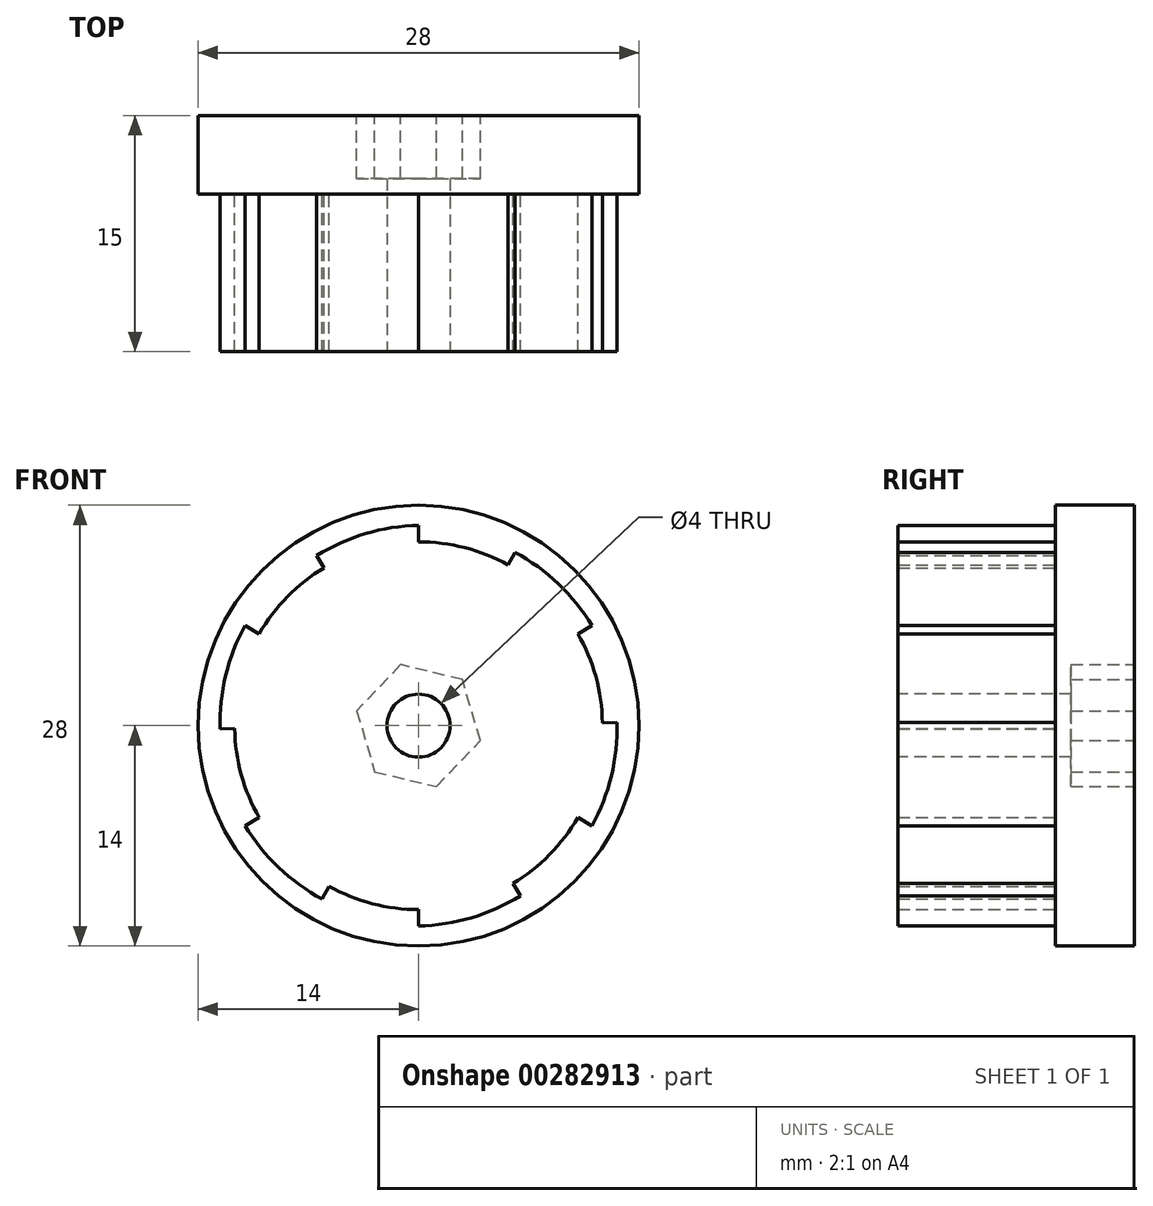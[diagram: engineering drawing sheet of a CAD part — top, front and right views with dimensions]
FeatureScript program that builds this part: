
annotation { "Feature Type Name" : "Feature", "Feature Type Description" : "" }
export const myFeature = defineFeature(function(context is Context, id is Id, definition is map)
    precondition{}
    {
        {
            var Q0;
            Q0=qCreatedBy(makeId("Front.planeOp"),FACE);
            var sketch = newSketch(context, id + "F0", { "sketchPlane" : qUnion([Q0])});
            skCircle(sketch, "E0", {"center": v(0, 0) * mm, "radius": 12.9 * mm, "construction": true});
            skCircle(sketch, "E1", {"center": v(0, 0) * mm, "radius": 14 * mm, "construction": true});
            skCircle(sketch, "E2", {"center": v(0, 0) * mm, "radius": 11.9 * mm, "construction": true});
            skCircle(sketch, "E3", {"center": v(0, 0) * mm, "radius": 11.68 * mm});
            skLineSegment(sketch, "E4", {"start": v(0, 0) * mm, "end": v(0, 14) * mm, "construction": true});
            skLineSegment(sketch, "E5", {"start": v(0, 0) * mm, "end": v(-7.2, 12.01) * mm, "construction": true});
            skLineSegment(sketch, "E6", {"start": v(-6, 10.02) * mm, "end": v(-6.47, 10.8) * mm});
            skLineSegment(sketch, "E7", {"start": v(0, 11.68) * mm, "end": v(0, 12.72) * mm});
            skArc(sketch, "E8", {"start": v(0, 12.72) * mm, "mid": v(-3.36, 12.2) * mm, "end": v(-6.47, 10.8) * mm});
            skLineSegment(sketch, "E9.1.0", {"start": v(-11.68, -0.19) * mm, "end": v(-12.6, -0.2) * mm});
            skArc(sketch, "E9.1.1", {"start": v(-11.02, 6.36) * mm, "mid": v(-12.24, 3.19) * mm, "end": v(-12.6, -0.2) * mm});
            skLineSegment(sketch, "E9.1.2", {"start": v(-10.12, 5.84) * mm, "end": v(-11.02, 6.36) * mm});
            skLineSegment(sketch, "E9.2.0", {"start": v(-5.68, -10.2) * mm, "end": v(-6.12, -11) * mm});
            skArc(sketch, "E9.2.1", {"start": v(-11.02, -6.36) * mm, "mid": v(-8.88, -9.01) * mm, "end": v(-6.12, -11) * mm});
            skLineSegment(sketch, "E9.2.2", {"start": v(-10.12, -5.84) * mm, "end": v(-11.02, -6.36) * mm});
            skLineSegment(sketch, "E9.3.0", {"start": v(6, -10.02) * mm, "end": v(6.47, -10.8) * mm});
            skArc(sketch, "E9.3.1", {"start": v(0, -12.72) * mm, "mid": v(3.36, -12.2) * mm, "end": v(6.47, -10.8) * mm});
            skLineSegment(sketch, "E9.3.2", {"start": v(0, -11.68) * mm, "end": v(0, -12.72) * mm});
            skLineSegment(sketch, "E9.4.0", {"start": v(11.68, 0.19) * mm, "end": v(12.6, 0.2) * mm});
            skArc(sketch, "E9.4.1", {"start": v(11.02, -6.36) * mm, "mid": v(12.24, -3.19) * mm, "end": v(12.6, 0.2) * mm});
            skLineSegment(sketch, "E9.4.2", {"start": v(10.12, -5.84) * mm, "end": v(11.02, -6.36) * mm});
            skLineSegment(sketch, "E9.5.0", {"start": v(5.68, 10.2) * mm, "end": v(6.12, 11) * mm});
            skArc(sketch, "E9.5.1", {"start": v(11.02, 6.36) * mm, "mid": v(8.88, 9.01) * mm, "end": v(6.12, 11) * mm});
            skLineSegment(sketch, "E9.5.2", {"start": v(10.12, 5.84) * mm, "end": v(11.02, 6.36) * mm});
            skSolve(sketch);
        }
        {
            var Q0;
            Q0 = qSketchRegion(id + "F0", true);
            extrude(context, id + "F1", {"entities" : qUnion([Q0]), "depth" : 10 * mm});
        }
        {
            var Q0;
            Q0=makeQuery(id+"F1.opExtrude","CAP_FACE",FACE,{"disambiguationData":[OSD([sQuery(id+"F0.wireOp",EDGE,"E3"),sQuery(id+"F0.wireOp",EDGE,"E6"),sQuery(id+"F0.wireOp",EDGE,"E7"),sQuery(id+"F0.wireOp",EDGE,"E8"),sQuery(id+"F0.wireOp",EDGE,"E9.1.0"),sQuery(id+"F0.wireOp",EDGE,"E9.1.1"),sQuery(id+"F0.wireOp",EDGE,"E9.1.2"),sQuery(id+"F0.wireOp",EDGE,"E9.2.0"),sQuery(id+"F0.wireOp",EDGE,"E9.2.1"),sQuery(id+"F0.wireOp",EDGE,"E9.2.2"),sQuery(id+"F0.wireOp",EDGE,"E9.3.0"),sQuery(id+"F0.wireOp",EDGE,"E9.3.1"),sQuery(id+"F0.wireOp",EDGE,"E9.3.2"),sQuery(id+"F0.wireOp",EDGE,"E9.4.0"),sQuery(id+"F0.wireOp",EDGE,"E9.4.1"),sQuery(id+"F0.wireOp",EDGE,"E9.4.2"),sQuery(id+"F0.wireOp",EDGE,"E9.5.0"),sQuery(id+"F0.wireOp",EDGE,"E9.5.1"),sQuery(id+"F0.wireOp",EDGE,"E9.5.2")])],"isStart":false});
            var sketch = newSketch(context, id + "F2", { "sketchPlane" : qUnion([Q0])});
            skCircle(sketch, "E10", {"center": v(0, 0) * mm, "radius": 2 * mm});
            skSolve(sketch);
        }
        {
            var Q0;
            Q0=makeQuery(id+"F1.opExtrude","CAP_FACE",FACE,{"disambiguationData":[OSD([sQuery(id+"F0.wireOp",EDGE,"E3"),sQuery(id+"F0.wireOp",EDGE,"E6"),sQuery(id+"F0.wireOp",EDGE,"E7"),sQuery(id+"F0.wireOp",EDGE,"E8"),sQuery(id+"F0.wireOp",EDGE,"E9.1.0"),sQuery(id+"F0.wireOp",EDGE,"E9.1.1"),sQuery(id+"F0.wireOp",EDGE,"E9.1.2"),sQuery(id+"F0.wireOp",EDGE,"E9.2.0"),sQuery(id+"F0.wireOp",EDGE,"E9.2.1"),sQuery(id+"F0.wireOp",EDGE,"E9.2.2"),sQuery(id+"F0.wireOp",EDGE,"E9.3.0"),sQuery(id+"F0.wireOp",EDGE,"E9.3.1"),sQuery(id+"F0.wireOp",EDGE,"E9.3.2"),sQuery(id+"F0.wireOp",EDGE,"E9.4.0"),sQuery(id+"F0.wireOp",EDGE,"E9.4.1"),sQuery(id+"F0.wireOp",EDGE,"E9.4.2"),sQuery(id+"F0.wireOp",EDGE,"E9.5.0"),sQuery(id+"F0.wireOp",EDGE,"E9.5.1"),sQuery(id+"F0.wireOp",EDGE,"E9.5.2")])],"isStart":true});
            var sketch = newSketch(context, id + "F3", { "sketchPlane" : qUnion([Q0])});
            skCircle(sketch, "E11", {"center": v(0, 0) * mm, "radius": 14 * mm});
            skSolve(sketch);
        }
        {
            var Q0;
            Q0 = qSketchRegion(id + "F3", true);
            extrude(context, id + "F4", {"entities" : qUnion([Q0]), "operationType" : NewBodyOperationType.ADD, "depth" : 5 * mm});
        }
        {
            var Q0;
            Q0 = qSketchRegion(id + "F2", true);
            extrude(context, id + "F5", {"entities" : qUnion([Q0]), "operationType" : NewBodyOperationType.REMOVE, "oppositeDirection" : true, "depth" : 40 * mm});
        }
        {
            var Q0;
            Q0=makeQuery(id+"F4.opExtrude","CAP_FACE",FACE,{"disambiguationData":[OSD([sQuery(id+"F3.wireOp",EDGE,"E11")])],"isStart":false});
            var sketch = newSketch(context, id + "F6", { "sketchPlane" : qUnion([Q0])});
            skCircle(sketch, "E12.cCircle", {"center": v(0, 0) * mm, "radius": 3.5 * mm, "construction": true});
            skLineSegment(sketch, "E12.0", {"start": v(-2.78, 2.93) * mm, "end": v(1.15, 3.87) * mm});
            skLineSegment(sketch, "E12.1", {"start": v(1.15, 3.87) * mm, "end": v(3.93, 0.94) * mm});
            skLineSegment(sketch, "E12.2", {"start": v(3.93, 0.94) * mm, "end": v(2.78, -2.93) * mm});
            skLineSegment(sketch, "E12.3", {"start": v(2.78, -2.93) * mm, "end": v(-1.15, -3.87) * mm});
            skLineSegment(sketch, "E12.4", {"start": v(-1.15, -3.87) * mm, "end": v(-3.93, -0.94) * mm});
            skLineSegment(sketch, "E12.5", {"start": v(-3.93, -0.94) * mm, "end": v(-2.78, 2.93) * mm});
            skPoint(sketch, "E12.0.midPoint", {"position": v(-0.82, 3.4) * mm});
            skSolve(sketch);
        }
        {
            var Q0;
            Q0 = qSketchRegion(id + "F6", true);
            extrude(context, id + "F7", {"entities" : qUnion([Q0]), "operationType" : NewBodyOperationType.REMOVE, "oppositeDirection" : true, "depth" : 4 * mm});
        }
    });
